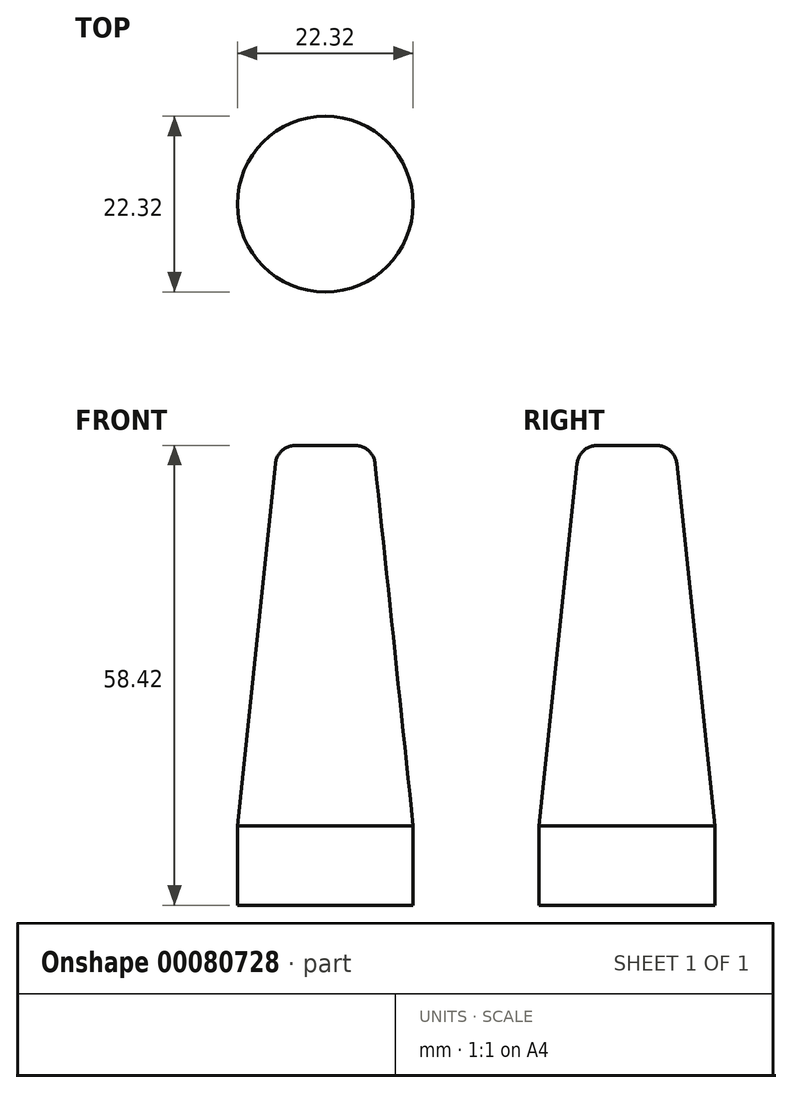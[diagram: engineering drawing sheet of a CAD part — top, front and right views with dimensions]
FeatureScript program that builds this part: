
annotation { "Feature Type Name" : "Feature", "Feature Type Description" : "" }
export const myFeature = defineFeature(function(context is Context, id is Id, definition is map)
    precondition{}
    {
        {
            var Q0;
            Q0=qCreatedBy(makeId("Top.planeOp"),FACE);
            var sketch = newSketch(context, id + "F0", { "sketchPlane" : qUnion([Q0])});
            skCircle(sketch, "E0", {"center": v(0, 0) * mm, "radius": 11.16 * mm});
            skSolve(sketch);
        }
        {
            var Q0;
            Q0=makeQuery(id+"F0.imprint","IMPRINT",FACE,{"disambiguationData":[TD([[makeQuery(id+"F0.imprint","IMPRINT",EDGE,{"derivedFrom":sQuery(id+"F0.wireOp",EDGE,"E0")}),1.0]])]});
            extrude(context, id + "F1", {"entities" : qUnion([Q0]), "depth" : 58.42 * mm});
        }
        {
            var Q0;
            Q0=makeQuery(id+"F1.opExtrude","CAP_EDGE",EDGE,{"disambiguationData":[OSD([sQuery(id+"F0.wireOp",EDGE,"E0")])],"isStart":false});
            chamfer(context, id + "F2", {"entities" : qUnion([Q0]), "chamferType" : ChamferType.OFFSET_ANGLE, "width" : 5.08 * mm, "oppositeDirection" : false, "angle" : 84 * degree, "tangentPropagation" : true});
        }
        {
            var Q0;
            {var subQ0=sQuery(id+"F0.wireOp",EDGE,"E0");Q0=makeQuery(id+"F2.opChamfer","BLEND_EDGE",EDGE,{"blendedFrom":[makeQuery(id+"F1.opExtrude","CAP_EDGE",EDGE,{"disambiguationData":[OSD([subQ0])],"isStart":false}),makeQuery(id+"F1.opExtrude","CAP_FACE",FACE,{"disambiguationData":[OSD([subQ0])],"isStart":false})],"blendedInto":[makeQuery(id+"F1.opExtrude","CAP_FACE",FACE,{"disambiguationData":[OSD([subQ0])],"isStart":false})]});}
            fillet(context, id + "F3", {"entities" : qUnion([Q0]), "radius" : 2.54 * mm, "tangentPropagation" : true, "allowEdgeOverflow" : false});
        }
    });
